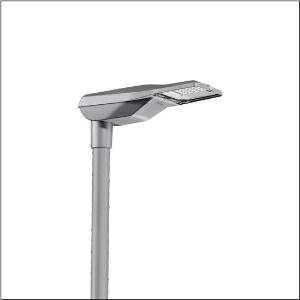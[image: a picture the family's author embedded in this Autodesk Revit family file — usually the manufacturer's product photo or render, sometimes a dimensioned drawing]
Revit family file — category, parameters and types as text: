
# Revit family: streetlight_sl_21_iq_micro___st0_8a_5xe1c41d08db_9d18
name_source: partatom
category: Lighting Fixtures
units: mm (PartAtom-declared; Revit-internal decimal feet)

## family parameters
Cut with Voids When Loaded = No
Host = Face
Light Source = No
Part Type = Normal
Room Calculation Point = No
Round Connector Dimension = Use Diameter
Shared = No

## types (1)
- --- (1 x LED, 5010 lm, 36.4 W, 4000K)
    Apparent Load = 36 VA
    CIE Flux Codes = 38 75 97 100 100
    Color Rendering = 70
    Color Temperature = 4000K
    Default Elevation = 1800 mm
    Description = Streetlight SL 21 iQ micro, mast luminaire, primary light control with lens, of PMMA, primary optical cover: cover, of toughened safety glass, transparent, light distribution: ST0.8a, light emission: direct distribution, primary light characteristic: asymmetric, installation type: post-top, side-entry, LED, High Power LED, rated luminous flux: 5.010lm, luminous efficacy: 138lm/W, light colour: 740, colour temperature: 4000K, control: Auto-Match, Temp-Guard, Lumen-Switch, Night-Set, Smart-Wire, Light-Fading, Desk-Remote (wireless, voltage-free reading and setting of iQ features in the workshop via application-optimized NFC function/RFID function), optimised constant luminous flux control (CLO 2.0), presetting dimming linear, mains connection: 220..240V, AC, 50/60Hz, start of lifetime: 36W, end of service life: 38W, reduction: 16W, luminaire housing, of diecast aluminium, powder-coated, Siteco® metallic grey (DB 702S), corrosivity category C5 mid according to DIN EN ISO 12944, please order mast flange separately, inclination adjustable: 0°, 5°, 10°, 15°, sealing non-destructively replaceable, multi-level sealing system, length: 528mm, width: 235mm, height: 110mm, mast flange for spigot size: 42mm (side-entry): 5XC10008XM4, 60/48mm (side-entry/post-top): 5XC10108XM2, 76/60mm (side-entry/post-top): 5XC10108XM1, protection rating (complete): IP66, insulation class (complete): insulation class II (safety insulation), certification: CE, ENEC, ENEC+, VDE, impact resistance: IK09, permissible operating ambient temperature for outdoor applications: -40..+50°C, standard-compliant lighting for roads and squares, packaging unit: 1 piece

Light Distribution: ST0.8a
    Height = 110 mm
    Lamp = 1 x LED
    Lamp Light Flux = 5010 lm
    Lamp Power = 36.4 W
    Lamp count = 1
    Length = 528 mm
    Luminous efficacy = 138 lm/W
    Manufacturer = Siteco
    ModVariant = No
    Model = 5XE1C41D08DB
    Number of Poles = 1
    OnlyDefault = Yes
    Power Factor = 1
    Product Name = Streetlight SL 21 iQ micro | ST0.8a
    Product group = mast luminaire | pylon top
    ProductGroupID = 6100
    Protection Class = Protection class II
    Protection Degree = IP 66
    RLX_Detail_Level = 1
    RLX_Emergency_Light_Flux = 0 lm
    RLX_Emergency_Type = 0
    RLX_Emergency_Type_DB = No
    RlxData = <blob elided: 98689 chars, md5=414884ac>
    Socket = socket
    Standby Power = 0 W
    System Light Flux = 5010 lm
    System Power = 36 W
    Type Comments = factory setting: luminous flux: 100 % | dim-lin: 254 | 715 mA
    Type Image = l_1006881.jpg
    URL = http://relux.com
    VarID = @adj_086807
    Voltage = 0 V
    Weight = 0.00 kg
    Width = 235 mm

## geometry (parser evidence)
native form markers: Blend x4, Sweep x11
no freeform markers — native parametric forms only
